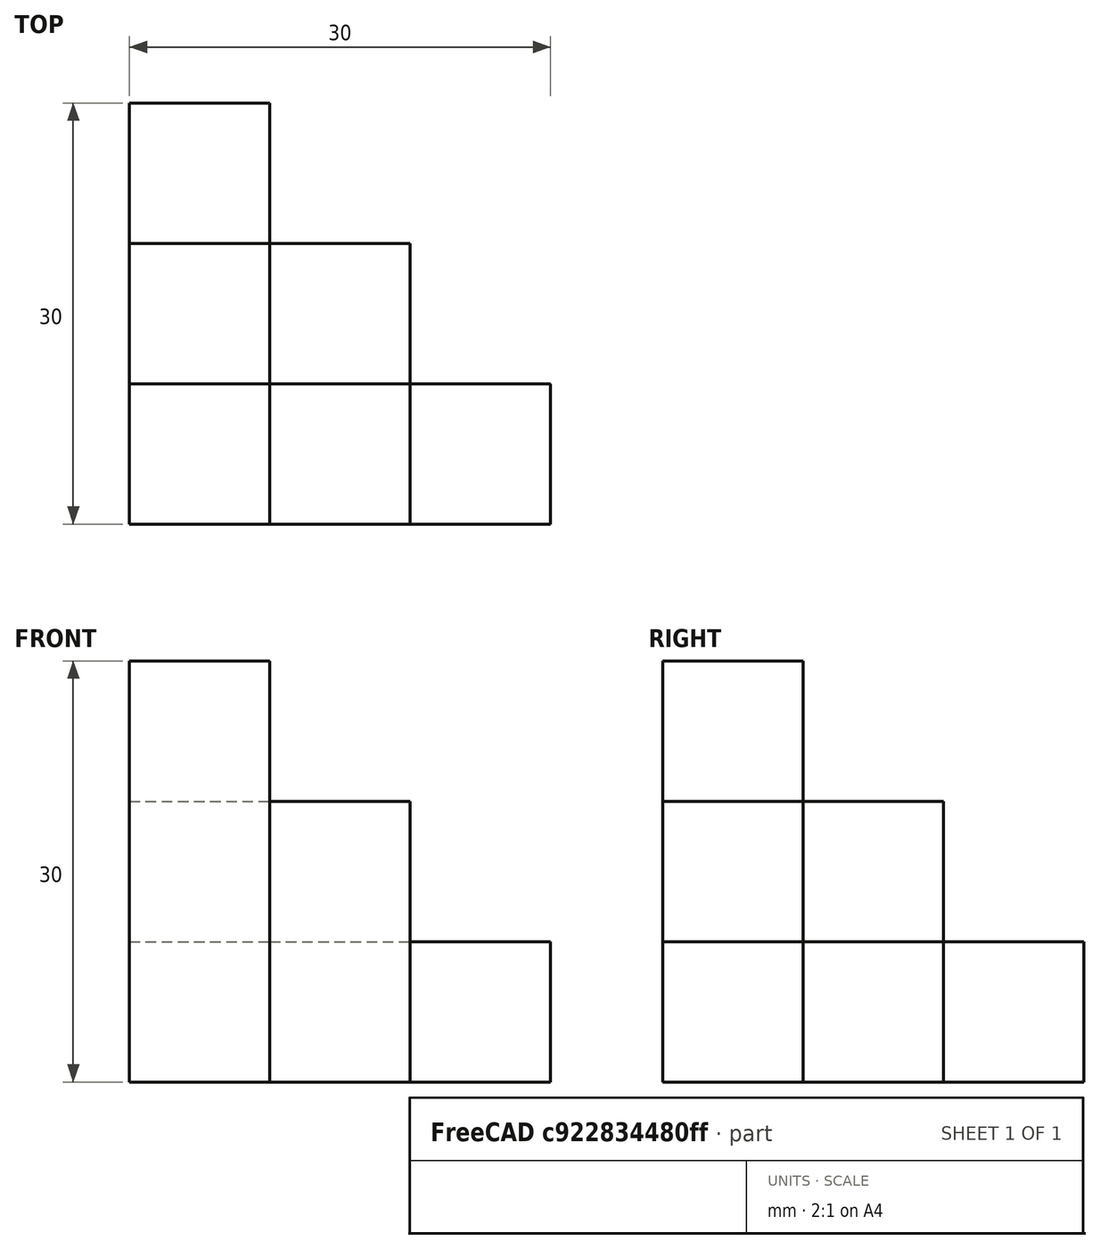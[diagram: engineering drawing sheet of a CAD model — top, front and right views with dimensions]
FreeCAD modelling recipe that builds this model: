
FCSTD DOCUMENT  (FreeCAD 0.14R3702 (Git))
Label: cubo piramide
License: CC-BY 3.0
LicenseURL: http://creativecommons.org/licenses/by/3.0/
objects: Part::Box×6
note: 6 computed .brp shape members not serialized (recipe doc carries the construction recipe); baked Part::Feature solids carry a one-line shape summary decoded from their .brp

FEATURE [Part::Box] Box  label="Cubo30"
  Height = 30
  Length = 10
  Width = 10
FEATURE [Part::Box] Box001  label="Cubo20-1"
  Height = 20
  Length = 10
  Placement = pos=(10,0,0) rot=(0,0,1;0rad)
  Width = 10
FEATURE [Part::Box] Box002  label="Cubo20-2"
  Height = 20
  Length = 10
  Placement = pos=(0,10,0) rot=(0,0,1;0rad)
  Width = 10
FEATURE [Part::Box] Box003  label="cubo 10-1"
  Height = 10
  Length = 10
  Placement = pos=(10,10,0) rot=(0,0,1;0rad)
  Width = 10
FEATURE [Part::Box] Box004  label="cubo 10-2"
  Height = 10
  Length = 10
  Placement = pos=(0,20,0) rot=(0,0,1;0rad)
  Width = 10
FEATURE [Part::Box] Box005  label="cubo 10-3"
  Height = 10
  Length = 10
  Placement = pos=(20,0,0) rot=(0,0,1;0rad)
  Width = 10
